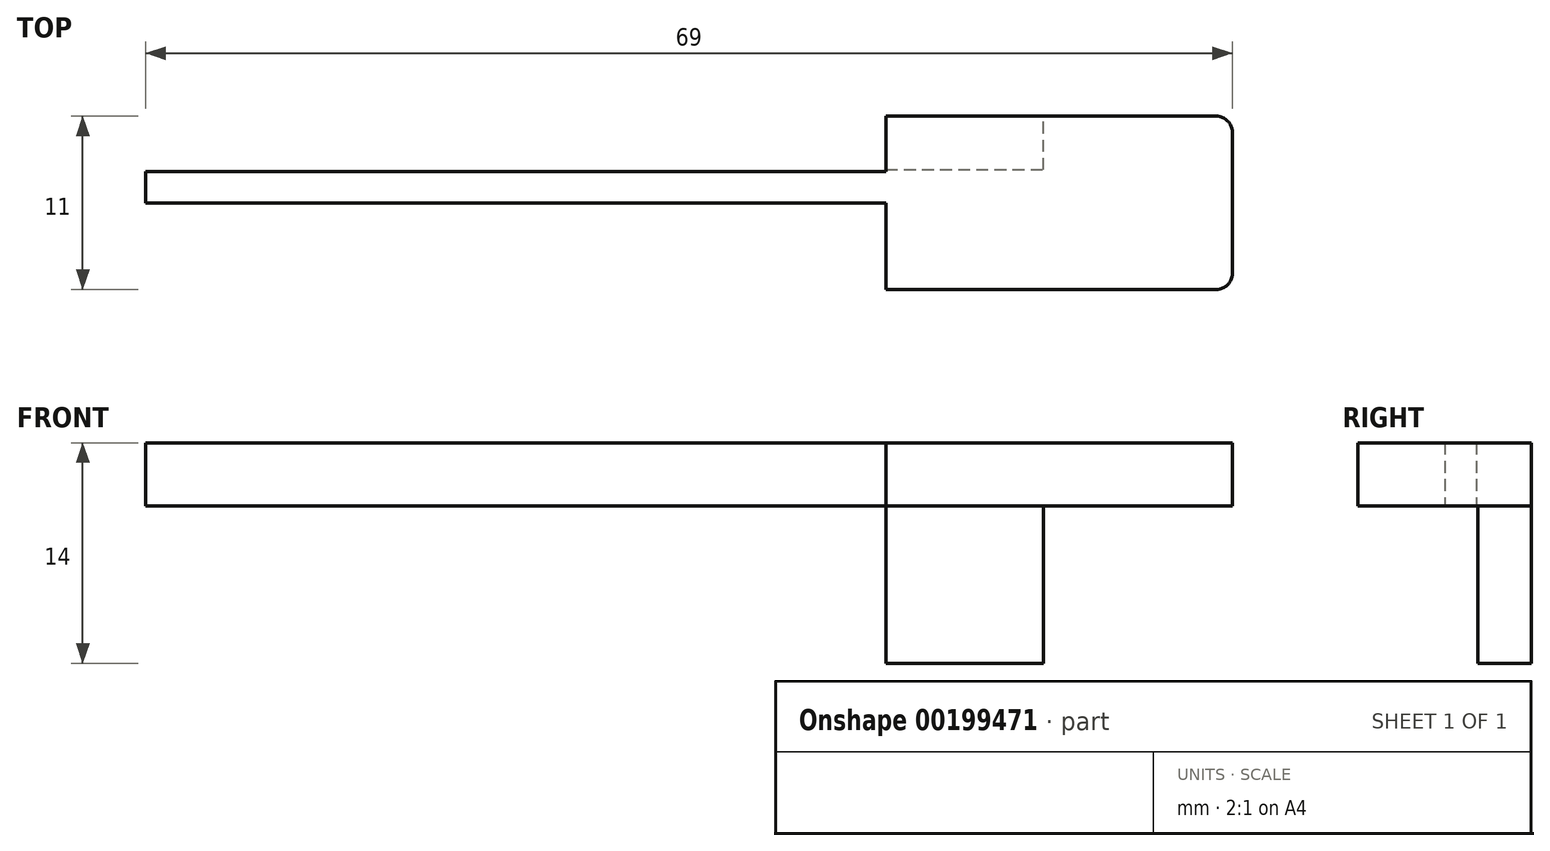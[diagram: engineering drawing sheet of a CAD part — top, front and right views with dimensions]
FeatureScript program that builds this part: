
annotation { "Feature Type Name" : "Feature", "Feature Type Description" : "" }
export const myFeature = defineFeature(function(context is Context, id is Id, definition is map)
    precondition{}
    {
        {
            var Q0;
            Q0=qCreatedBy(makeId("Top.planeOp"),FACE);
            var sketch = newSketch(context, id + "F0", { "sketchPlane" : qUnion([Q0])});
            skLineSegment(sketch, "E0.bottom", {"start": v(-36.1, 10.56) * mm, "end": v(10.9, 10.56) * mm});
            skLineSegment(sketch, "E0.top", {"start": v(-36.1, 8.56) * mm, "end": v(10.9, 8.56) * mm});
            skLineSegment(sketch, "E0.left", {"start": v(-36.1, 10.56) * mm, "end": v(-36.1, 8.56) * mm});
            skLineSegment(sketch, "E0.right", {"start": v(10.9, 10.56) * mm, "end": v(10.9, 8.56) * mm});
            skLineSegment(sketch, "E1.bottom", {"start": v(32.9, 14.06) * mm, "end": v(10.9, 14.06) * mm});
            skLineSegment(sketch, "E1.top", {"start": v(32.9, 3.06) * mm, "end": v(10.9, 3.06) * mm});
            skLineSegment(sketch, "E1.left", {"start": v(32.9, 14.06) * mm, "end": v(32.9, 3.06) * mm});
            skLineSegment(sketch, "E1.right", {"start": v(10.9, 14.06) * mm, "end": v(10.9, 3.06) * mm});
            skLineSegment(sketch, "E2.bottom", {"start": v(10.9, 10.66) * mm, "end": v(20.9, 10.66) * mm});
            skLineSegment(sketch, "E2.top", {"start": v(10.9, 14.06) * mm, "end": v(20.9, 14.06) * mm});
            skLineSegment(sketch, "E2.left", {"start": v(10.9, 10.66) * mm, "end": v(10.9, 14.06) * mm});
            skLineSegment(sketch, "E2.right", {"start": v(20.9, 10.66) * mm, "end": v(20.9, 14.06) * mm});
            skSolve(sketch);
        }
        {
            var Q0;
            {var subQ0=sQuery(id+"F0.wireOp",EDGE,"E0.left");Q0=makeQuery(id+"F0.imprint","IMPRINT",FACE,{"disambiguationData":[TD([[makeQuery(id+"F0.imprint","IMPRINT",EDGE,{"derivedFrom":subQ0}),1.0]])]});}
            var Q1;
            {var subQ0=sQuery(id+"F0.wireOp",EDGE,"E0.right");Q1=makeQuery(id+"F0.imprint","IMPRINT",FACE,{"disambiguationData":[TD([[makeQuery(id+"F0.imprint","IMPRINT",EDGE,{"derivedFrom":subQ0}),-1.0]])]});}
            var Q2;
            {var subQ0=sQuery(id+"F0.wireOp",EDGE,"E0.right");Q2=makeQuery(id+"F0.imprint","IMPRINT",FACE,{"disambiguationData":[TD([[makeQuery(id+"F0.imprint","IMPRINT",EDGE,{"derivedFrom":subQ0}),1.0]])]});}
            var Q3;
            Q3=makeQuery(id+"F0.imprint","IMPRINT",FACE,{"disambiguationData":[TD([[makeQuery(id+"F0.imprint","IMPRINT",EDGE,{"derivedFrom":sQuery(id+"F0.wireOp",EDGE,"E2.bottom")}),1.0]])]});
            var Q4;
            Q4=makeQuery(id+"F0.imprint","IMPRINT",FACE,{"disambiguationData":[TD([[makeQuery(id+"F0.imprint","IMPRINT",EDGE,{"derivedFrom":sQuery(id+"F0.wireOp",EDGE,"E1.bottom")}),1.0]])]});
            extrude(context, id + "F1", {"entities" : qUnion([Q0, Q1, Q2, Q3, Q4]), "depth" : 4 * mm});
        }
        {
            var Q0;
            Q0=makeQuery(id+"F0.imprint","IMPRINT",FACE,{"disambiguationData":[TD([[makeQuery(id+"F0.imprint","IMPRINT",EDGE,{"derivedFrom":sQuery(id+"F0.wireOp",EDGE,"E2.bottom")}),1.0]])]});
            extrude(context, id + "F2", {"entities" : qUnion([Q0]), "operationType" : NewBodyOperationType.ADD, "oppositeDirection" : true, "depth" : 10 * mm});
        }
        {
            var Q0;
            Q0=makeQuery(id+"F1.opExtrude","SWEPT_EDGE",EDGE,{"disambiguationData":[OSD([sQuery(id+"F0.wireOp",EDGE,"E1.top"),sQuery(id+"F0.wireOp",EDGE,"E1.left")])]});
            var Q1;
            Q1=makeQuery(id+"F1.opExtrude","SWEPT_EDGE",EDGE,{"disambiguationData":[OSD([sQuery(id+"F0.wireOp",EDGE,"E1.bottom"),sQuery(id+"F0.wireOp",EDGE,"E1.left")])]});
            fillet(context, id + "F3", {"entities" : qUnion([Q0, Q1]), "radius" : 1 * mm, "tangentPropagation" : true, "allowEdgeOverflow" : false});
        }
    });
